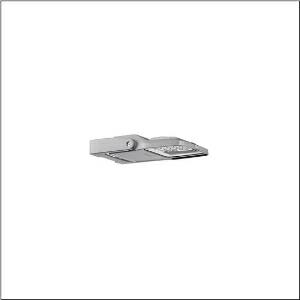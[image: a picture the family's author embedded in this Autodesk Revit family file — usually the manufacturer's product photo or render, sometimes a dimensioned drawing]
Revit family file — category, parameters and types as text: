
# Revit family: floodlight_fl_21_iq_micro___pl33t_5xa7761a4f2a_c8ff
name_source: partatom
category: Lighting Fixtures
units: mm (PartAtom-declared; Revit-internal decimal feet)

## family parameters
Cut with Voids When Loaded = No
Host = Face
Light Source = No
Part Type = Normal
Room Calculation Point = No
Round Connector Dimension = Use Diameter
Shared = No

## types (1)
- --- (1 x LED, 3050 lm, 23.1 W, 4000K)
    Apparent Load = 23 VA
    CIE Flux Codes = 26 75 99 100 100
    Color Rendering = 70
    Color Temperature = 4000K
    Default Elevation = 1800 mm
    Description = Floodlight FL 21 iQ micro, floodlight, primary light control with lens, of PMMA, primary optical cover: protective disc, of toughened safety glass, transparent, light distribution: PL33T, light emission: direct distribution, installation type: surface-mounted, lamps: LED, High Power LED, rated values: 3.050lm | 23,1W | 132lm/W (begin service life); end service life: 3.050lm | 23,8W; at 50% lumin. flux: 1.525lm | 11W | 138,6lm/W, colour temperature: 4000K, colour rendering: CRI > 70, light colour: 740, light setting 1 begin service life: 100% | 3.050lm | 23,1W | 132lm/W | 4.000K, light setting 1 end service life: 23,8W, further light settings possible, control: optimised constant luminous flux control (CLO 2.0), Desk-Remote (wireless, voltage-free reading and setting of iQ features in the workshop via application-optimized NFC function/RFID function), Light-Fading, Smart-Wire, Night-Set, Lumen-Switch, Temp-Guard, Auto-Match, pre-setting: linear dimming characteristic, with terminal, 6-pole, mains connection: 220..240V, AC, 50/60Hz, luminaire housing, of diecast aluminium, powder-coated, SITECO metallic grey (DB 702S), corrosivity category C5 mid according to DIN EN ISO 12944suitable for swimming poolschlorine-resistant, sealing non-destructively replaceable, design bracket, of diecast aluminium, powder-coated, SITECO metallic grey (DB 702S), protection rating (complete): IP66, insulation class (complete): insulation class II (safety insulation), certification: CE, ENEC, VDE, protection symbol: D, impact resistance: IK07, permissible operating ambient temperature: -40..+40°C, permissible operating ambient temperature for outdoor applications: -40..+50°C, standard: DIN EN 12944, LABS conformity tested according to VDMA 24364:2018-05, packaging unit: 1 piece

Light Distribution: PL33T
    Height = 65 mm
    Lamp = 1 x LED
    Lamp Light Flux = 3050 lm
    Lamp Power = 23.1 W
    Lamp count = 1
    Length = 312 mm
    Luminous efficacy = 132 lm/W
    Manufacturer = Siteco
    ModVariant = No
    Model = 5XA7761A4F2A
    Mounting Place = Wall
    Mounting Type = Surface mounted
    Number of Poles = 1
    OnlyDefault = Yes
    Power Factor = 1
    Product Name = Floodlight FL 21 iQ micro | PL33T
    Product group = floodlight | wall mounted
    ProductGroupID = 2002
    Protection Class = Protection class II
    Protection Degree = IP 66
    RLX_Detail_Level = 1
    RLX_Emergency_Light_Flux = 0 lm
    RLX_Emergency_Type = 0
    RLX_Emergency_Type_DB = No
    RlxData = <blob elided: 97637 chars, md5=dd262e33>
    Socket = socket
    Standby Power = 0 W
    System Light Flux = 3050 lm
    System Power = 23 W
    Type Comments = factory setting: luminous flux: 100 % | dim-lin: 254 | 455 mA
    Type Image = l_1006878.jpg
    URL = http://relux.com
    VarID = @adj_147641
    Voltage = 0 V
    Weight = 0.00 kg
    Width = 230 mm

## geometry (parser evidence)
native form markers: Blend x4, Sweep x13
no freeform markers — native parametric forms only
